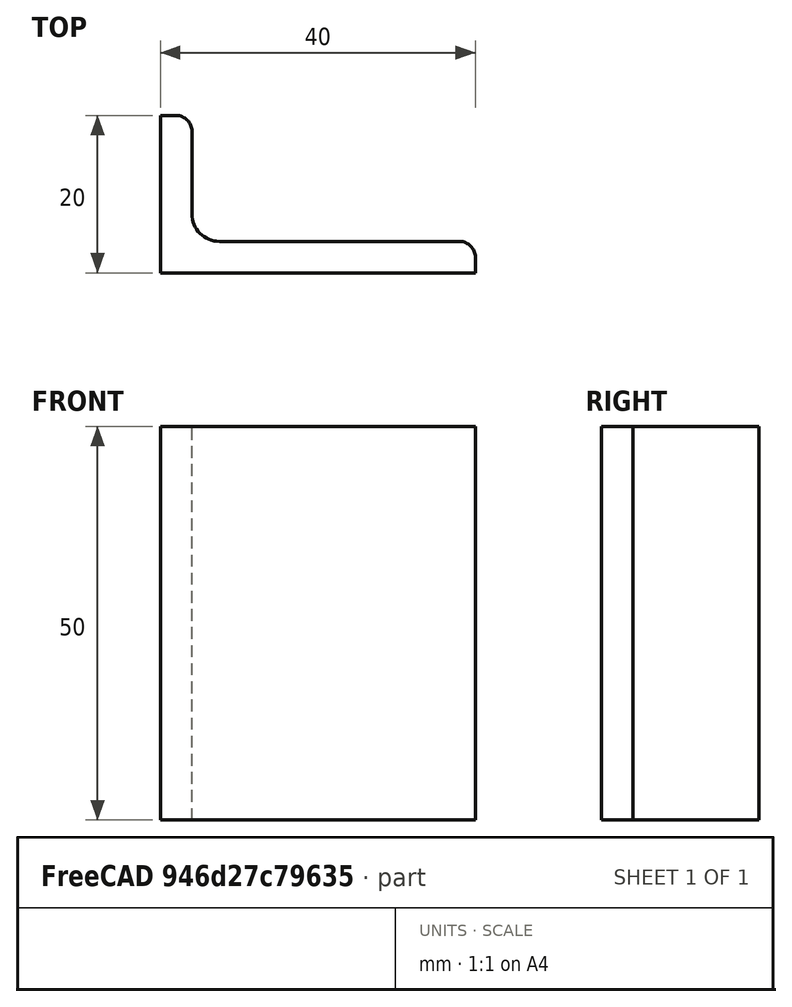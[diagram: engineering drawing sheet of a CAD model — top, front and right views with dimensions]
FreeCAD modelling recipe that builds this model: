
FCSTD DOCUMENT  (FreeCAD 0.15R4671 (Git))
Label: Angle Bar 40x20x4 EN10056 S235JR
License: All rights reserved
LicenseURL: http://en.wikipedia.org/wiki/All_rights_reserved
objects: Sketcher::SketchObject×1, Part::Extrusion×1
note: 2 computed .brp shape members not serialized (recipe doc carries the construction recipe); baked Part::Feature solids carry a one-line shape summary decoded from their .brp

FEATURE [Sketcher::SketchObject] Sketch
  sketch-geometry (9):
    g0: LineSegment StartX=0 StartY=0 StartZ=0 EndX=40 EndY=0 EndZ=0
    g1: LineSegment StartX=40 StartY=0 StartZ=0 EndX=40 EndY=2 EndZ=0
    g2: LineSegment StartX=38 StartY=4 StartZ=0 EndX=7.5 EndY=4 EndZ=0
    g3: LineSegment StartX=0 StartY=0 StartZ=0 EndX=0 EndY=20 EndZ=0
    g4: LineSegment StartX=0 StartY=20 StartZ=0 EndX=2 EndY=20 EndZ=0
    g5: LineSegment StartX=4 StartY=18 StartZ=0 EndX=4 EndY=7.5 EndZ=0
    g6: ArcOfCircle CenterX=7.5 CenterY=7.5 CenterZ=0 NormalX=0 NormalY=0 NormalZ=1 Radius=3.5 StartAngle=3.14159 EndAngle=4.71239
    g7: ArcOfCircle CenterX=2 CenterY=18 CenterZ=0 NormalX=0 NormalY=0 NormalZ=1 Radius=2 StartAngle=0 EndAngle=1.5708
    g8: ArcOfCircle CenterX=38 CenterY=2 CenterZ=0 NormalX=0 NormalY=0 NormalZ=1 Radius=2 StartAngle=0 EndAngle=1.5708
  constraints (23):
    c: Coincident(g0,g-1)
    c: Horizontal(g0)
    c: Coincident(g1,g0)
    c: Vertical(g1)
    c: Horizontal(g2)
    c: Coincident(g3,g-1)
    c: Vertical(g3)
    c: Coincident(g4,g3)
    c: Horizontal(g4)
    c: Vertical(g5)
    c: Tangent(g5,g6) = -1.5708
    c: Tangent(g2,g6) = 1.5708
    c: Tangent(g4,g7) = 1.5708
    c: Tangent(g5,g7) = 1.5708
    c: Tangent(g2,g8) = -1.5708
    c: Tangent(g1,g8) = -1.5708
    c: DistanceX(g0) = 40
    c: DistanceY(g3) = 20
    c: DistanceY(g0,g2) = 4
    c: DistanceX(g3,g5) = 4
    c: Radius(g6) = 3.5
    c: Radius(g8) = 2
    c: Radius(g7) = 2
FEATURE [Part::Extrusion] Extrude  label="Angle Bar 40x20x4 EN10056 S235JR"
  Base = -> Sketch
  Dir = (0,0,50)
  Solid = true
